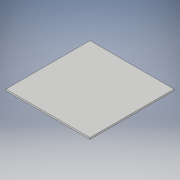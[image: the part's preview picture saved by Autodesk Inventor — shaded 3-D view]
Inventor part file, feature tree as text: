
AUTODESK INVENTOR PART (.ipt)
format: ipt  version: 2018.3 (Build 223284000, 284)  size: 89,600 bytes
history: native  units: in
note: dims shown in document units (in); Inventor stores cm internally (conversion verified against a paired STEP export)
features: extrude x1, sketch x1
ambient origin geometry x8: Origin, YZ Plane, XZ Plane, XY Plane, X Axis, Y Axis, Z Axis, Center Point
bodies: Solid1 (feature_tree)
feature tree (2):
  extrude  "Extrusion1"  Depth=13.0in
  sketch  "Sketch1"  dims[d0=13.0in d1=13.0in d2=0.25in d3=0.0in]
